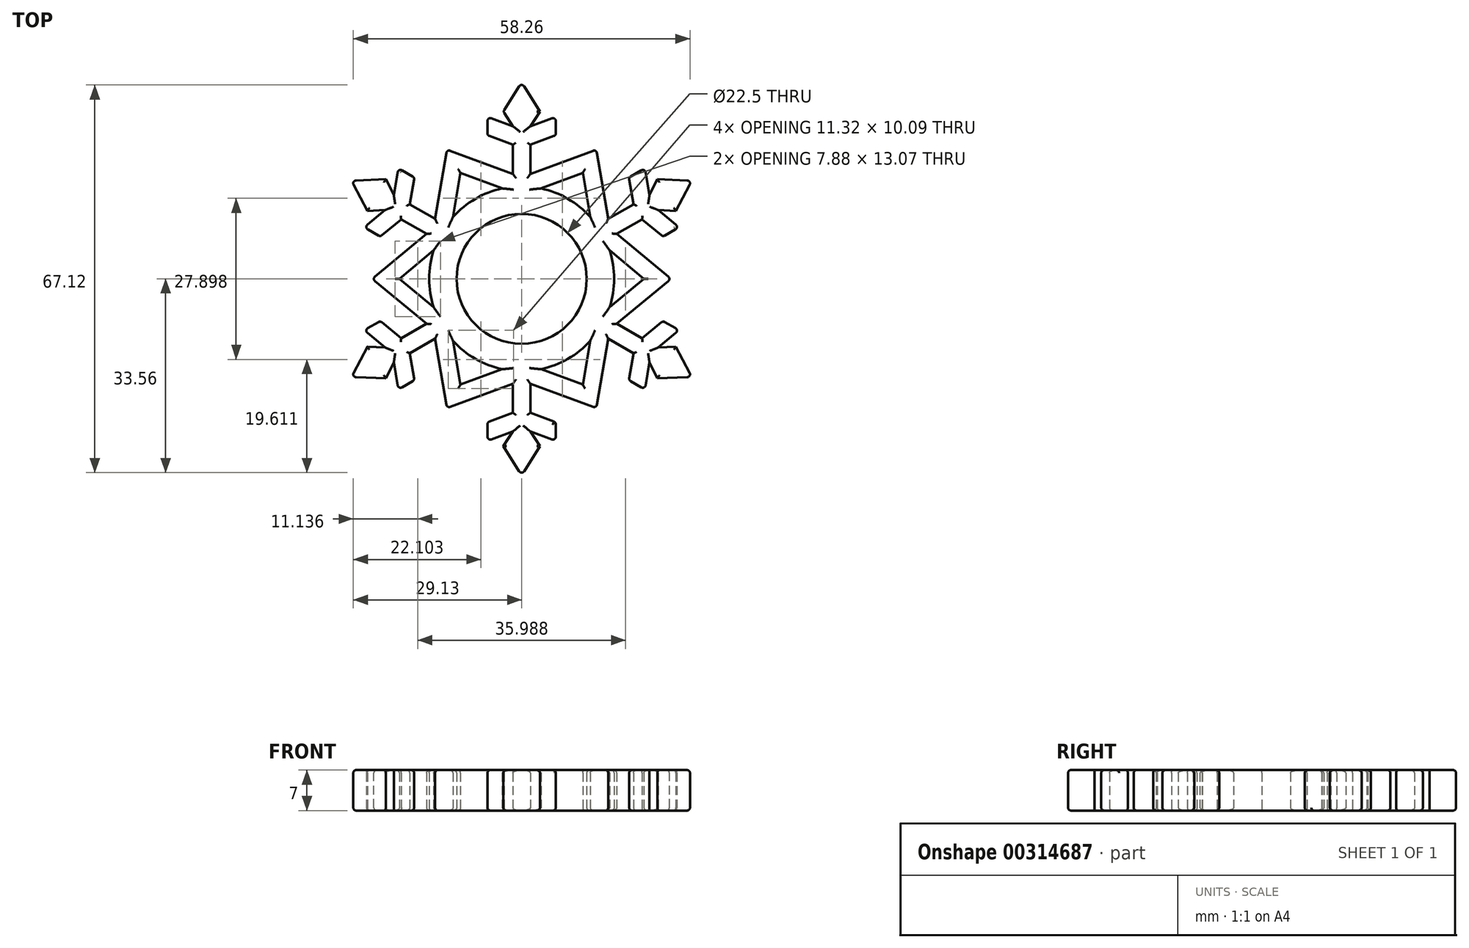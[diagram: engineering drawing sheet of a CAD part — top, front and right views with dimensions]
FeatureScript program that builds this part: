
annotation { "Feature Type Name" : "Feature", "Feature Type Description" : "" }
export const myFeature = defineFeature(function(context is Context, id is Id, definition is map)
    precondition{}
    {
        {
            var Q0;
            Q0=qCreatedBy(makeId("Top.planeOp"),FACE);
            var sketch = newSketch(context, id + "F0", { "sketchPlane" : qUnion([Q0])});
            skCircle(sketch, "E0", {"center": v(0, 0) * mm, "radius": 11.25 * mm});
            skCircle(sketch, "E1", {"center": v(0, 0) * mm, "radius": 16 * mm});
            skCircle(sketch, "E2", {"center": v(0, 0) * mm, "radius": 34 * mm, "construction": true});
            skPoint(sketch, "E3.0.midPoint", {"position": v(19.02, -6.18) * mm});
            skLineSegment(sketch, "E4", {"start": v(29.44, -17) * mm, "end": v(-29.44, 17) * mm, "construction": true});
            skLineSegment(sketch, "E5", {"start": v(29.44, 17) * mm, "end": v(-29.44, -17) * mm, "construction": true});
            skLineSegment(sketch, "E6", {"start": v(0, 34) * mm, "end": v(0, -34) * mm, "construction": true});
            skCircle(sketch, "E7.cCircle", {"center": v(0, 0) * mm, "radius": 23.5 * mm, "construction": true});
            skLineSegment(sketch, "E7.0", {"start": v(11.75, -20.35) * mm, "end": v(-11.75, -20.35) * mm, "construction": true});
            skLineSegment(sketch, "E7.1", {"start": v(-11.75, -20.35) * mm, "end": v(-23.5, 0) * mm, "construction": true});
            skLineSegment(sketch, "E7.2", {"start": v(-23.5, 0) * mm, "end": v(-11.75, 20.35) * mm, "construction": true});
            skLineSegment(sketch, "E7.3", {"start": v(-11.75, 20.35) * mm, "end": v(11.75, 20.35) * mm, "construction": true});
            skLineSegment(sketch, "E7.4", {"start": v(11.75, 20.35) * mm, "end": v(23.5, 0) * mm, "construction": true});
            skLineSegment(sketch, "E7.5", {"start": v(23.5, 0) * mm, "end": v(11.75, -20.35) * mm, "construction": true});
            skLineSegment(sketch, "E8", {"start": v(-11.75, 20.35) * mm, "end": v(0, 16) * mm, "construction": true});
            skLineSegment(sketch, "E9", {"start": v(-12.92, 22.39) * mm, "end": v(0, 17.6) * mm});
            skLineSegment(sketch, "E10", {"start": v(-3.36, 15.64) * mm, "end": v(-10.58, 18.32) * mm});
            skLineSegment(sketch, "E11", {"start": v(-11.75, 20.35) * mm, "end": v(-13.86, 8) * mm, "construction": true});
            skLineSegment(sketch, "E12", {"start": v(-11.87, 10.73) * mm, "end": v(-10.58, 18.32) * mm});
            skLineSegment(sketch, "E13", {"start": v(-12.92, 22.39) * mm, "end": v(-15.24, 8.8) * mm});
            skPoint(sketch, "E14.orphan", {"position": v(-16.07, 20.35) * mm});
            skLineSegment(sketch, "E15.1.0", {"start": v(-25.85, 0) * mm, "end": v(-15.24, -8.8) * mm});
            skLineSegment(sketch, "E15.1.1", {"start": v(-25.85, 0) * mm, "end": v(-15.24, 8.8) * mm});
            skLineSegment(sketch, "E15.1.2", {"start": v(-15.23, 4.91) * mm, "end": v(-21.15, 0) * mm});
            skLineSegment(sketch, "E15.1.3", {"start": v(-15.23, -4.91) * mm, "end": v(-21.15, 0) * mm});
            skLineSegment(sketch, "E15.2.0", {"start": v(-12.92, -22.39) * mm, "end": v(0, -17.6) * mm});
            skLineSegment(sketch, "E15.2.1", {"start": v(-12.92, -22.39) * mm, "end": v(-15.24, -8.8) * mm});
            skLineSegment(sketch, "E15.2.2", {"start": v(-11.87, -10.73) * mm, "end": v(-10.58, -18.32) * mm});
            skLineSegment(sketch, "E15.2.3", {"start": v(-3.36, -15.64) * mm, "end": v(-10.58, -18.32) * mm});
            skLineSegment(sketch, "E16.2.3.0", {"start": v(12.92, -22.39) * mm, "end": v(15.24, -8.8) * mm});
            skLineSegment(sketch, "E16.3.3.0", {"start": v(12.92, -22.39) * mm, "end": v(0, -17.6) * mm});
            skLineSegment(sketch, "E16.6.3.0", {"start": v(3.36, -15.64) * mm, "end": v(10.58, -18.32) * mm});
            skLineSegment(sketch, "E16.9.3.0", {"start": v(11.87, -10.73) * mm, "end": v(10.58, -18.32) * mm});
            skLineSegment(sketch, "E16.2.4.0", {"start": v(25.85, 0) * mm, "end": v(15.24, 8.8) * mm});
            skLineSegment(sketch, "E16.3.4.0", {"start": v(25.85, 0) * mm, "end": v(15.24, -8.8) * mm});
            skLineSegment(sketch, "E16.6.4.0", {"start": v(15.23, -4.91) * mm, "end": v(21.15, 0) * mm});
            skLineSegment(sketch, "E16.9.4.0", {"start": v(15.23, 4.91) * mm, "end": v(21.15, 0) * mm});
            skLineSegment(sketch, "E16.2.5.0", {"start": v(12.92, 22.39) * mm, "end": v(0, 17.6) * mm});
            skLineSegment(sketch, "E16.3.5.0", {"start": v(12.92, 22.39) * mm, "end": v(15.24, 8.8) * mm});
            skLineSegment(sketch, "E16.6.5.0", {"start": v(11.87, 10.73) * mm, "end": v(10.58, 18.32) * mm});
            skLineSegment(sketch, "E16.9.5.0", {"start": v(3.36, 15.64) * mm, "end": v(10.58, 18.32) * mm});
            skLineSegment(sketch, "E17", {"start": v(0, 34) * mm, "end": v(-3.17, 28.97) * mm});
            skLineSegment(sketch, "E18", {"start": v(-3.17, 28.97) * mm, "end": v(-1.5, 26.4) * mm});
            skLineSegment(sketch, "E19", {"start": v(-1.5, 26.4) * mm, "end": v(-5.91, 28.04) * mm});
            skLineSegment(sketch, "E20", {"start": v(-5.91, 28.04) * mm, "end": v(-5.91, 24.84) * mm});
            skLineSegment(sketch, "E21", {"start": v(-5.91, 24.84) * mm, "end": v(-1.5, 23.21) * mm});
            skLineSegment(sketch, "E22", {"start": v(-1.5, 23.21) * mm, "end": v(-1.5, 18.16) * mm});
            skLineSegment(sketch, "E23.MirrorCS", {"start": v(0, 34) * mm, "end": v(3.17, 28.97) * mm});
            skLineSegment(sketch, "E24.MirrorCS", {"start": v(3.17, 28.97) * mm, "end": v(1.5, 26.4) * mm});
            skLineSegment(sketch, "E25.MirrorCS", {"start": v(1.5, 26.4) * mm, "end": v(5.91, 28.04) * mm});
            skLineSegment(sketch, "E26.MirrorCS", {"start": v(5.91, 28.04) * mm, "end": v(5.91, 24.84) * mm});
            skLineSegment(sketch, "E27.MirrorCS", {"start": v(5.91, 24.84) * mm, "end": v(1.5, 23.21) * mm});
            skLineSegment(sketch, "E28.MirrorCS", {"start": v(1.5, 23.21) * mm, "end": v(1.5, 18.16) * mm});
            skLineSegment(sketch, "E29.1.0", {"start": v(-29.44, 17) * mm, "end": v(-26.67, 11.74) * mm});
            skLineSegment(sketch, "E29.1.1", {"start": v(-29.44, 17) * mm, "end": v(-23.5, 17.23) * mm});
            skLineSegment(sketch, "E29.1.2", {"start": v(-23.5, 17.23) * mm, "end": v(-22.12, 14.5) * mm});
            skLineSegment(sketch, "E29.1.3", {"start": v(-26.67, 11.74) * mm, "end": v(-23.62, 11.9) * mm});
            skLineSegment(sketch, "E29.1.4", {"start": v(-23.62, 11.9) * mm, "end": v(-27.24, 8.9) * mm});
            skLineSegment(sketch, "E29.1.5", {"start": v(-27.24, 8.9) * mm, "end": v(-24.47, 7.3) * mm});
            skLineSegment(sketch, "E29.1.6", {"start": v(-24.47, 7.3) * mm, "end": v(-20.85, 10.3) * mm});
            skLineSegment(sketch, "E29.1.7", {"start": v(-20.85, 10.3) * mm, "end": v(-16.47, 7.78) * mm});
            skLineSegment(sketch, "E29.1.8", {"start": v(-19.35, 12.9) * mm, "end": v(-14.97, 10.38) * mm});
            skLineSegment(sketch, "E29.1.9", {"start": v(-18.56, 17.54) * mm, "end": v(-19.35, 12.9) * mm});
            skLineSegment(sketch, "E29.1.10", {"start": v(-21.33, 19.14) * mm, "end": v(-18.56, 17.54) * mm});
            skLineSegment(sketch, "E29.1.11", {"start": v(-22.12, 14.5) * mm, "end": v(-21.33, 19.14) * mm});
            skLineSegment(sketch, "E29.2.0", {"start": v(-29.44, -17) * mm, "end": v(-23.5, -17.23) * mm});
            skLineSegment(sketch, "E29.2.1", {"start": v(-29.44, -17) * mm, "end": v(-26.67, -11.74) * mm});
            skLineSegment(sketch, "E29.2.2", {"start": v(-26.67, -11.74) * mm, "end": v(-23.62, -11.9) * mm});
            skLineSegment(sketch, "E29.2.3", {"start": v(-23.5, -17.23) * mm, "end": v(-22.12, -14.5) * mm});
            skLineSegment(sketch, "E29.2.4", {"start": v(-22.12, -14.5) * mm, "end": v(-21.33, -19.14) * mm});
            skLineSegment(sketch, "E29.2.5", {"start": v(-21.33, -19.14) * mm, "end": v(-18.56, -17.54) * mm});
            skLineSegment(sketch, "E29.2.6", {"start": v(-18.56, -17.54) * mm, "end": v(-19.35, -12.9) * mm});
            skLineSegment(sketch, "E29.2.7", {"start": v(-19.35, -12.9) * mm, "end": v(-14.97, -10.38) * mm});
            skLineSegment(sketch, "E29.2.8", {"start": v(-20.85, -10.3) * mm, "end": v(-16.47, -7.78) * mm});
            skLineSegment(sketch, "E29.2.9", {"start": v(-24.47, -7.3) * mm, "end": v(-20.85, -10.3) * mm});
            skLineSegment(sketch, "E29.2.10", {"start": v(-27.24, -8.9) * mm, "end": v(-24.47, -7.3) * mm});
            skLineSegment(sketch, "E29.2.11", {"start": v(-23.62, -11.9) * mm, "end": v(-27.24, -8.9) * mm});
            skLineSegment(sketch, "E29.3.0", {"start": v(0, -34) * mm, "end": v(3.17, -28.97) * mm});
            skLineSegment(sketch, "E29.3.1", {"start": v(0, -34) * mm, "end": v(-3.17, -28.97) * mm});
            skLineSegment(sketch, "E29.3.2", {"start": v(-3.17, -28.97) * mm, "end": v(-1.5, -26.4) * mm});
            skLineSegment(sketch, "E29.3.3", {"start": v(3.17, -28.97) * mm, "end": v(1.5, -26.4) * mm});
            skLineSegment(sketch, "E29.3.4", {"start": v(1.5, -26.4) * mm, "end": v(5.91, -28.04) * mm});
            skLineSegment(sketch, "E29.3.5", {"start": v(5.91, -28.04) * mm, "end": v(5.91, -24.84) * mm});
            skLineSegment(sketch, "E29.3.6", {"start": v(5.91, -24.84) * mm, "end": v(1.5, -23.21) * mm});
            skLineSegment(sketch, "E29.3.7", {"start": v(1.5, -23.21) * mm, "end": v(1.5, -18.16) * mm});
            skLineSegment(sketch, "E29.3.8", {"start": v(-1.5, -23.21) * mm, "end": v(-1.5, -18.16) * mm});
            skLineSegment(sketch, "E29.3.9", {"start": v(-5.91, -24.84) * mm, "end": v(-1.5, -23.21) * mm});
            skLineSegment(sketch, "E29.3.10", {"start": v(-5.91, -28.04) * mm, "end": v(-5.91, -24.84) * mm});
            skLineSegment(sketch, "E29.3.11", {"start": v(-1.5, -26.4) * mm, "end": v(-5.91, -28.04) * mm});
            skLineSegment(sketch, "E29.4.0", {"start": v(29.44, -17) * mm, "end": v(26.67, -11.74) * mm});
            skLineSegment(sketch, "E29.4.1", {"start": v(29.44, -17) * mm, "end": v(23.5, -17.23) * mm});
            skLineSegment(sketch, "E29.4.2", {"start": v(23.5, -17.23) * mm, "end": v(22.12, -14.5) * mm});
            skLineSegment(sketch, "E29.4.3", {"start": v(26.67, -11.74) * mm, "end": v(23.62, -11.9) * mm});
            skLineSegment(sketch, "E29.4.4", {"start": v(23.62, -11.9) * mm, "end": v(27.24, -8.9) * mm});
            skLineSegment(sketch, "E29.4.5", {"start": v(27.24, -8.9) * mm, "end": v(24.47, -7.3) * mm});
            skLineSegment(sketch, "E29.4.6", {"start": v(24.47, -7.3) * mm, "end": v(20.85, -10.3) * mm});
            skLineSegment(sketch, "E29.4.7", {"start": v(20.85, -10.3) * mm, "end": v(16.47, -7.78) * mm});
            skLineSegment(sketch, "E29.4.8", {"start": v(19.35, -12.9) * mm, "end": v(14.97, -10.38) * mm});
            skLineSegment(sketch, "E29.4.9", {"start": v(18.56, -17.54) * mm, "end": v(19.35, -12.9) * mm});
            skLineSegment(sketch, "E29.4.10", {"start": v(21.33, -19.14) * mm, "end": v(18.56, -17.54) * mm});
            skLineSegment(sketch, "E29.4.11", {"start": v(22.12, -14.5) * mm, "end": v(21.33, -19.14) * mm});
            skLineSegment(sketch, "E29.5.0", {"start": v(29.44, 17) * mm, "end": v(23.5, 17.23) * mm});
            skLineSegment(sketch, "E29.5.1", {"start": v(29.44, 17) * mm, "end": v(26.67, 11.74) * mm});
            skLineSegment(sketch, "E29.5.2", {"start": v(26.67, 11.74) * mm, "end": v(23.62, 11.9) * mm});
            skLineSegment(sketch, "E29.5.3", {"start": v(23.5, 17.23) * mm, "end": v(22.12, 14.5) * mm});
            skLineSegment(sketch, "E29.5.4", {"start": v(22.12, 14.5) * mm, "end": v(21.33, 19.14) * mm});
            skLineSegment(sketch, "E29.5.5", {"start": v(21.33, 19.14) * mm, "end": v(18.56, 17.54) * mm});
            skLineSegment(sketch, "E29.5.6", {"start": v(18.56, 17.54) * mm, "end": v(19.35, 12.9) * mm});
            skLineSegment(sketch, "E29.5.7", {"start": v(19.35, 12.9) * mm, "end": v(14.97, 10.38) * mm});
            skLineSegment(sketch, "E29.5.8", {"start": v(20.85, 10.3) * mm, "end": v(16.47, 7.78) * mm});
            skLineSegment(sketch, "E29.5.9", {"start": v(24.47, 7.3) * mm, "end": v(20.85, 10.3) * mm});
            skLineSegment(sketch, "E29.5.10", {"start": v(27.24, 8.9) * mm, "end": v(24.47, 7.3) * mm});
            skLineSegment(sketch, "E29.5.11", {"start": v(23.62, 11.9) * mm, "end": v(27.24, 8.9) * mm});
            skSolve(sketch);
        }
        {
            var Q0;
            Q0=makeQuery(id+"F0.imprint","IMPRINT",FACE,{"disambiguationData":[TD([[makeQuery(id+"F0.imprint","IMPRINT",EDGE,{"derivedFrom":sQuery(id+"F0.wireOp",EDGE,"E17")}),1.0]])]});
            var Q1;
            {var subQ23=sQuery(id+"F0.wireOp",EDGE,"E10");Q1=makeQuery(id+"F0.imprint","IMPRINT",FACE,{"disambiguationData":[TD([[makeQuery(id+"F0.imprint","IMPRINT",EDGE,{"derivedFrom":subQ23}),-1.0]])]});}
            var Q2;
            Q2=makeQuery(id+"F0.imprint","IMPRINT",FACE,{"disambiguationData":[TD([[makeQuery(id+"F0.imprint","IMPRINT",EDGE,{"derivedFrom":sQuery(id+"F0.wireOp",EDGE,"E0")}),-1.0]])]});
            var Q3;
            Q3=makeQuery(id+"F0.imprint","IMPRINT",FACE,{"disambiguationData":[TD([[makeQuery(id+"F0.imprint","IMPRINT",EDGE,{"derivedFrom":sQuery(id+"F0.wireOp",EDGE,"E29.1.0")}),1.0]])]});
            var Q4;
            Q4=makeQuery(id+"F0.imprint","IMPRINT",FACE,{"disambiguationData":[TD([[makeQuery(id+"F0.imprint","IMPRINT",EDGE,{"derivedFrom":sQuery(id+"F0.wireOp",EDGE,"E29.5.0")}),1.0]])]});
            var Q5;
            Q5=makeQuery(id+"F0.imprint","IMPRINT",FACE,{"disambiguationData":[TD([[makeQuery(id+"F0.imprint","IMPRINT",EDGE,{"derivedFrom":sQuery(id+"F0.wireOp",EDGE,"E29.4.0")}),1.0]])]});
            var Q6;
            Q6=makeQuery(id+"F0.imprint","IMPRINT",FACE,{"disambiguationData":[TD([[makeQuery(id+"F0.imprint","IMPRINT",EDGE,{"derivedFrom":sQuery(id+"F0.wireOp",EDGE,"E29.2.0")}),1.0]])]});
            var Q7;
            Q7=makeQuery(id+"F0.imprint","IMPRINT",FACE,{"disambiguationData":[TD([[makeQuery(id+"F0.imprint","IMPRINT",EDGE,{"derivedFrom":sQuery(id+"F0.wireOp",EDGE,"E29.3.0")}),1.0]])]});
            extrude(context, id + "F1", {"entities" : qUnion([Q0, Q1, Q2, Q3, Q4, Q5, Q6, Q7]), "depth" : 7 * mm, "offsetDistance" : 25 * mm});
        }
        {
            var Q0;
            Q0=makeQuery(id+"F1.opExtrude","SWEPT_EDGE",EDGE,{"disambiguationData":[OSD([sQuery(id+"F0.wireOp",EDGE,"E29.4.0"),sQuery(id+"F0.wireOp",EDGE,"E29.4.1")])]});
            var Q1;
            Q1=makeQuery(id+"F1.opExtrude","SWEPT_EDGE",EDGE,{"disambiguationData":[OSD([sQuery(id+"F0.wireOp",EDGE,"E29.4.4"),sQuery(id+"F0.wireOp",EDGE,"E29.4.5")])]});
            var Q2;
            Q2=makeQuery(id+"F1.opExtrude","SWEPT_EDGE",EDGE,{"disambiguationData":[OSD([sQuery(id+"F0.wireOp",EDGE,"E16.2.4.0"),sQuery(id+"F0.wireOp",EDGE,"E16.3.4.0")])]});
            var Q3;
            Q3=makeQuery(id+"F1.opExtrude","SWEPT_EDGE",EDGE,{"disambiguationData":[OSD([sQuery(id+"F0.wireOp",EDGE,"E29.5.10"),sQuery(id+"F0.wireOp",EDGE,"E29.5.11")])]});
            var Q4;
            Q4=makeQuery(id+"F1.opExtrude","SWEPT_EDGE",EDGE,{"disambiguationData":[OSD([sQuery(id+"F0.wireOp",EDGE,"E29.5.0"),sQuery(id+"F0.wireOp",EDGE,"E29.5.1")])]});
            var Q5;
            Q5=makeQuery(id+"F1.opExtrude","SWEPT_EDGE",EDGE,{"disambiguationData":[OSD([sQuery(id+"F0.wireOp",EDGE,"E29.5.4"),sQuery(id+"F0.wireOp",EDGE,"E29.5.5")])]});
            var Q6;
            Q6=makeQuery(id+"F1.opExtrude","SWEPT_EDGE",EDGE,{"disambiguationData":[OSD([sQuery(id+"F0.wireOp",EDGE,"E16.2.5.0"),sQuery(id+"F0.wireOp",EDGE,"E16.3.5.0")])]});
            var Q7;
            Q7=makeQuery(id+"F1.opExtrude","SWEPT_EDGE",EDGE,{"disambiguationData":[OSD([sQuery(id+"F0.wireOp",EDGE,"E25.MirrorCS"),sQuery(id+"F0.wireOp",EDGE,"E26.MirrorCS")])]});
            var Q8;
            Q8=makeQuery(id+"F1.opExtrude","SWEPT_EDGE",EDGE,{"disambiguationData":[OSD([sQuery(id+"F0.wireOp",EDGE,"E17"),sQuery(id+"F0.wireOp",EDGE,"E23.MirrorCS")])]});
            var Q9;
            Q9=makeQuery(id+"F1.opExtrude","SWEPT_EDGE",EDGE,{"disambiguationData":[OSD([sQuery(id+"F0.wireOp",EDGE,"E17"),sQuery(id+"F0.wireOp",EDGE,"E18")])]});
            var Q10;
            Q10=makeQuery(id+"F1.opExtrude","SWEPT_EDGE",EDGE,{"disambiguationData":[OSD([sQuery(id+"F0.wireOp",EDGE,"E19"),sQuery(id+"F0.wireOp",EDGE,"E20")])]});
            var Q11;
            Q11=makeQuery(id+"F1.opExtrude","SWEPT_EDGE",EDGE,{"disambiguationData":[OSD([sQuery(id+"F0.wireOp",EDGE,"E9"),sQuery(id+"F0.wireOp",EDGE,"E13")])]});
            var Q12;
            Q12=makeQuery(id+"F1.opExtrude","SWEPT_EDGE",EDGE,{"disambiguationData":[OSD([sQuery(id+"F0.wireOp",EDGE,"E29.1.10"),sQuery(id+"F0.wireOp",EDGE,"E29.1.11")])]});
            var Q13;
            Q13=makeQuery(id+"F1.opExtrude","SWEPT_EDGE",EDGE,{"disambiguationData":[OSD([sQuery(id+"F0.wireOp",EDGE,"E29.1.0"),sQuery(id+"F0.wireOp",EDGE,"E29.1.1")])]});
            var Q14;
            Q14=makeQuery(id+"F1.opExtrude","SWEPT_EDGE",EDGE,{"disambiguationData":[OSD([sQuery(id+"F0.wireOp",EDGE,"E29.1.4"),sQuery(id+"F0.wireOp",EDGE,"E29.1.5")])]});
            var Q15;
            Q15=makeQuery(id+"F1.opExtrude","SWEPT_EDGE",EDGE,{"disambiguationData":[OSD([sQuery(id+"F0.wireOp",EDGE,"E15.1.0"),sQuery(id+"F0.wireOp",EDGE,"E15.1.1")])]});
            var Q16;
            Q16=makeQuery(id+"F1.opExtrude","SWEPT_EDGE",EDGE,{"disambiguationData":[OSD([sQuery(id+"F0.wireOp",EDGE,"E29.2.10"),sQuery(id+"F0.wireOp",EDGE,"E29.2.11")])]});
            var Q17;
            Q17=makeQuery(id+"F1.opExtrude","SWEPT_EDGE",EDGE,{"disambiguationData":[OSD([sQuery(id+"F0.wireOp",EDGE,"E29.2.0"),sQuery(id+"F0.wireOp",EDGE,"E29.2.1")])]});
            var Q18;
            Q18=makeQuery(id+"F1.opExtrude","SWEPT_EDGE",EDGE,{"disambiguationData":[OSD([sQuery(id+"F0.wireOp",EDGE,"E29.2.4"),sQuery(id+"F0.wireOp",EDGE,"E29.2.5")])]});
            var Q19;
            Q19=makeQuery(id+"F1.opExtrude","SWEPT_EDGE",EDGE,{"disambiguationData":[OSD([sQuery(id+"F0.wireOp",EDGE,"E15.2.0"),sQuery(id+"F0.wireOp",EDGE,"E15.2.1")])]});
            var Q20;
            Q20=makeQuery(id+"F1.opExtrude","SWEPT_EDGE",EDGE,{"disambiguationData":[OSD([sQuery(id+"F0.wireOp",EDGE,"E29.3.10"),sQuery(id+"F0.wireOp",EDGE,"E29.3.11")])]});
            var Q21;
            Q21=makeQuery(id+"F1.opExtrude","SWEPT_EDGE",EDGE,{"disambiguationData":[OSD([sQuery(id+"F0.wireOp",EDGE,"E29.3.0"),sQuery(id+"F0.wireOp",EDGE,"E29.3.1")])]});
            var Q22;
            Q22=makeQuery(id+"F1.opExtrude","SWEPT_EDGE",EDGE,{"disambiguationData":[OSD([sQuery(id+"F0.wireOp",EDGE,"E29.3.4"),sQuery(id+"F0.wireOp",EDGE,"E29.3.5")])]});
            var Q23;
            Q23=makeQuery(id+"F1.opExtrude","SWEPT_EDGE",EDGE,{"disambiguationData":[OSD([sQuery(id+"F0.wireOp",EDGE,"E16.2.3.0"),sQuery(id+"F0.wireOp",EDGE,"E16.3.3.0")])]});
            var Q24;
            Q24=makeQuery(id+"F1.opExtrude","SWEPT_EDGE",EDGE,{"disambiguationData":[OSD([sQuery(id+"F0.wireOp",EDGE,"E29.4.10"),sQuery(id+"F0.wireOp",EDGE,"E29.4.11")])]});
            var Q25;
            Q25=makeQuery(id+"F1.opExtrude","SWEPT_EDGE",EDGE,{"disambiguationData":[OSD([sQuery(id+"F0.wireOp",EDGE,"E20"),sQuery(id+"F0.wireOp",EDGE,"E21")])]});
            var Q26;
            Q26=makeQuery(id+"F1.opExtrude","SWEPT_EDGE",EDGE,{"disambiguationData":[OSD([sQuery(id+"F0.wireOp",EDGE,"E26.MirrorCS"),sQuery(id+"F0.wireOp",EDGE,"E27.MirrorCS")])]});
            var Q27;
            Q27=makeQuery(id+"F1.opExtrude","SWEPT_EDGE",EDGE,{"disambiguationData":[OSD([sQuery(id+"F0.wireOp",EDGE,"E29.5.5"),sQuery(id+"F0.wireOp",EDGE,"E29.5.6")])]});
            var Q28;
            Q28=makeQuery(id+"F1.opExtrude","SWEPT_EDGE",EDGE,{"disambiguationData":[OSD([sQuery(id+"F0.wireOp",EDGE,"E29.5.9"),sQuery(id+"F0.wireOp",EDGE,"E29.5.10")])]});
            var Q29;
            Q29=makeQuery(id+"F1.opExtrude","SWEPT_EDGE",EDGE,{"disambiguationData":[OSD([sQuery(id+"F0.wireOp",EDGE,"E29.4.5"),sQuery(id+"F0.wireOp",EDGE,"E29.4.6")])]});
            var Q30;
            Q30=makeQuery(id+"F1.opExtrude","SWEPT_EDGE",EDGE,{"disambiguationData":[OSD([sQuery(id+"F0.wireOp",EDGE,"E29.4.9"),sQuery(id+"F0.wireOp",EDGE,"E29.4.10")])]});
            var Q31;
            Q31=makeQuery(id+"F1.opExtrude","SWEPT_EDGE",EDGE,{"disambiguationData":[OSD([sQuery(id+"F0.wireOp",EDGE,"E29.3.5"),sQuery(id+"F0.wireOp",EDGE,"E29.3.6")])]});
            var Q32;
            Q32=makeQuery(id+"F1.opExtrude","SWEPT_EDGE",EDGE,{"disambiguationData":[OSD([sQuery(id+"F0.wireOp",EDGE,"E29.3.9"),sQuery(id+"F0.wireOp",EDGE,"E29.3.10")])]});
            var Q33;
            Q33=makeQuery(id+"F1.opExtrude","SWEPT_EDGE",EDGE,{"disambiguationData":[OSD([sQuery(id+"F0.wireOp",EDGE,"E29.2.5"),sQuery(id+"F0.wireOp",EDGE,"E29.2.6")])]});
            var Q34;
            Q34=makeQuery(id+"F1.opExtrude","SWEPT_EDGE",EDGE,{"disambiguationData":[OSD([sQuery(id+"F0.wireOp",EDGE,"E29.2.9"),sQuery(id+"F0.wireOp",EDGE,"E29.2.10")])]});
            var Q35;
            Q35=makeQuery(id+"F1.opExtrude","SWEPT_EDGE",EDGE,{"disambiguationData":[OSD([sQuery(id+"F0.wireOp",EDGE,"E29.1.9"),sQuery(id+"F0.wireOp",EDGE,"E29.1.10")])]});
            var Q36;
            Q36=makeQuery(id+"F1.opExtrude","SWEPT_EDGE",EDGE,{"disambiguationData":[OSD([sQuery(id+"F0.wireOp",EDGE,"E29.1.5"),sQuery(id+"F0.wireOp",EDGE,"E29.1.6")])]});
            fillet(context, id + "F2", {"entities" : qUnion([Q0, Q1, Q2, Q3, Q4, Q5, Q6, Q7, Q8, Q9, Q10, Q11, Q12, Q13, Q14, Q15, Q16, Q17, Q18, Q19, Q20, Q21, Q22, Q23, Q24, Q25, Q26, Q27, Q28, Q29, Q30, Q31, Q32, Q33, Q34, Q35, Q36]), "radius" : .5 * mm, "tangentPropagation" : true, "allowEdgeOverflow" : false});
        }
        {
            var Q0;
            Q0=makeQuery(id+"F1.opExtrude","CAP_FACE",FACE,{"disambiguationData":[OSD([sQuery(id+"F0.wireOp",EDGE,"E0"),sQuery(id+"F0.wireOp",EDGE,"E1"),sQuery(id+"F0.wireOp",EDGE,"E9"),sQuery(id+"F0.wireOp",EDGE,"E10"),sQuery(id+"F0.wireOp",EDGE,"E12"),sQuery(id+"F0.wireOp",EDGE,"E13"),sQuery(id+"F0.wireOp",EDGE,"E15.1.0"),sQuery(id+"F0.wireOp",EDGE,"E15.1.1"),sQuery(id+"F0.wireOp",EDGE,"E15.1.2"),sQuery(id+"F0.wireOp",EDGE,"E15.1.3"),sQuery(id+"F0.wireOp",EDGE,"E15.2.0"),sQuery(id+"F0.wireOp",EDGE,"E15.2.1"),sQuery(id+"F0.wireOp",EDGE,"E15.2.2"),sQuery(id+"F0.wireOp",EDGE,"E15.2.3"),sQuery(id+"F0.wireOp",EDGE,"E16.2.3.0"),sQuery(id+"F0.wireOp",EDGE,"E16.3.3.0"),sQuery(id+"F0.wireOp",EDGE,"E16.6.3.0"),sQuery(id+"F0.wireOp",EDGE,"E16.9.3.0"),sQuery(id+"F0.wireOp",EDGE,"E16.2.4.0"),sQuery(id+"F0.wireOp",EDGE,"E16.3.4.0"),sQuery(id+"F0.wireOp",EDGE,"E16.6.4.0"),sQuery(id+"F0.wireOp",EDGE,"E16.9.4.0"),sQuery(id+"F0.wireOp",EDGE,"E16.2.5.0"),sQuery(id+"F0.wireOp",EDGE,"E16.3.5.0"),sQuery(id+"F0.wireOp",EDGE,"E16.6.5.0"),sQuery(id+"F0.wireOp",EDGE,"E16.9.5.0"),sQuery(id+"F0.wireOp",EDGE,"E17"),sQuery(id+"F0.wireOp",EDGE,"E18"),sQuery(id+"F0.wireOp",EDGE,"E19"),sQuery(id+"F0.wireOp",EDGE,"E20"),sQuery(id+"F0.wireOp",EDGE,"E21"),sQuery(id+"F0.wireOp",EDGE,"E22"),sQuery(id+"F0.wireOp",EDGE,"E23.MirrorCS"),sQuery(id+"F0.wireOp",EDGE,"E24.MirrorCS"),sQuery(id+"F0.wireOp",EDGE,"E25.MirrorCS"),sQuery(id+"F0.wireOp",EDGE,"E26.MirrorCS"),sQuery(id+"F0.wireOp",EDGE,"E27.MirrorCS"),sQuery(id+"F0.wireOp",EDGE,"E28.MirrorCS"),sQuery(id+"F0.wireOp",EDGE,"E29.1.0"),sQuery(id+"F0.wireOp",EDGE,"E29.1.1"),sQuery(id+"F0.wireOp",EDGE,"E29.1.2"),sQuery(id+"F0.wireOp",EDGE,"E29.1.3"),sQuery(id+"F0.wireOp",EDGE,"E29.1.4"),sQuery(id+"F0.wireOp",EDGE,"E29.1.5"),sQuery(id+"F0.wireOp",EDGE,"E29.1.6"),sQuery(id+"F0.wireOp",EDGE,"E29.1.7"),sQuery(id+"F0.wireOp",EDGE,"E29.1.8"),sQuery(id+"F0.wireOp",EDGE,"E29.1.9"),sQuery(id+"F0.wireOp",EDGE,"E29.1.10"),sQuery(id+"F0.wireOp",EDGE,"E29.1.11"),sQuery(id+"F0.wireOp",EDGE,"E29.2.0"),sQuery(id+"F0.wireOp",EDGE,"E29.2.1"),sQuery(id+"F0.wireOp",EDGE,"E29.2.2"),sQuery(id+"F0.wireOp",EDGE,"E29.2.3"),sQuery(id+"F0.wireOp",EDGE,"E29.2.4"),sQuery(id+"F0.wireOp",EDGE,"E29.2.5"),sQuery(id+"F0.wireOp",EDGE,"E29.2.6"),sQuery(id+"F0.wireOp",EDGE,"E29.2.7"),sQuery(id+"F0.wireOp",EDGE,"E29.2.8"),sQuery(id+"F0.wireOp",EDGE,"E29.2.9"),sQuery(id+"F0.wireOp",EDGE,"E29.2.10"),sQuery(id+"F0.wireOp",EDGE,"E29.2.11"),sQuery(id+"F0.wireOp",EDGE,"E29.3.0"),sQuery(id+"F0.wireOp",EDGE,"E29.3.1"),sQuery(id+"F0.wireOp",EDGE,"E29.3.2"),sQuery(id+"F0.wireOp",EDGE,"E29.3.3"),sQuery(id+"F0.wireOp",EDGE,"E29.3.4"),sQuery(id+"F0.wireOp",EDGE,"E29.3.5"),sQuery(id+"F0.wireOp",EDGE,"E29.3.6"),sQuery(id+"F0.wireOp",EDGE,"E29.3.7"),sQuery(id+"F0.wireOp",EDGE,"E29.3.8"),sQuery(id+"F0.wireOp",EDGE,"E29.3.9"),sQuery(id+"F0.wireOp",EDGE,"E29.3.10"),sQuery(id+"F0.wireOp",EDGE,"E29.3.11"),sQuery(id+"F0.wireOp",EDGE,"E29.4.0"),sQuery(id+"F0.wireOp",EDGE,"E29.4.1"),sQuery(id+"F0.wireOp",EDGE,"E29.4.2"),sQuery(id+"F0.wireOp",EDGE,"E29.4.3"),sQuery(id+"F0.wireOp",EDGE,"E29.4.4"),sQuery(id+"F0.wireOp",EDGE,"E29.4.5"),sQuery(id+"F0.wireOp",EDGE,"E29.4.6"),sQuery(id+"F0.wireOp",EDGE,"E29.4.7"),sQuery(id+"F0.wireOp",EDGE,"E29.4.8"),sQuery(id+"F0.wireOp",EDGE,"E29.4.9"),sQuery(id+"F0.wireOp",EDGE,"E29.4.10"),sQuery(id+"F0.wireOp",EDGE,"E29.4.11"),sQuery(id+"F0.wireOp",EDGE,"E29.5.0"),sQuery(id+"F0.wireOp",EDGE,"E29.5.1"),sQuery(id+"F0.wireOp",EDGE,"E29.5.2"),sQuery(id+"F0.wireOp",EDGE,"E29.5.3"),sQuery(id+"F0.wireOp",EDGE,"E29.5.4"),sQuery(id+"F0.wireOp",EDGE,"E29.5.5"),sQuery(id+"F0.wireOp",EDGE,"E29.5.6"),sQuery(id+"F0.wireOp",EDGE,"E29.5.7"),sQuery(id+"F0.wireOp",EDGE,"E29.5.8"),sQuery(id+"F0.wireOp",EDGE,"E29.5.9"),sQuery(id+"F0.wireOp",EDGE,"E29.5.10"),sQuery(id+"F0.wireOp",EDGE,"E29.5.11")])],"isStart":false});
            var Q1;
            Q1=makeQuery(id+"F1.opExtrude","CAP_FACE",FACE,{"disambiguationData":[OSD([sQuery(id+"F0.wireOp",EDGE,"E0"),sQuery(id+"F0.wireOp",EDGE,"E1"),sQuery(id+"F0.wireOp",EDGE,"E9"),sQuery(id+"F0.wireOp",EDGE,"E10"),sQuery(id+"F0.wireOp",EDGE,"E12"),sQuery(id+"F0.wireOp",EDGE,"E13"),sQuery(id+"F0.wireOp",EDGE,"E15.1.0"),sQuery(id+"F0.wireOp",EDGE,"E15.1.1"),sQuery(id+"F0.wireOp",EDGE,"E15.1.2"),sQuery(id+"F0.wireOp",EDGE,"E15.1.3"),sQuery(id+"F0.wireOp",EDGE,"E15.2.0"),sQuery(id+"F0.wireOp",EDGE,"E15.2.1"),sQuery(id+"F0.wireOp",EDGE,"E15.2.2"),sQuery(id+"F0.wireOp",EDGE,"E15.2.3"),sQuery(id+"F0.wireOp",EDGE,"E16.2.3.0"),sQuery(id+"F0.wireOp",EDGE,"E16.3.3.0"),sQuery(id+"F0.wireOp",EDGE,"E16.6.3.0"),sQuery(id+"F0.wireOp",EDGE,"E16.9.3.0"),sQuery(id+"F0.wireOp",EDGE,"E16.2.4.0"),sQuery(id+"F0.wireOp",EDGE,"E16.3.4.0"),sQuery(id+"F0.wireOp",EDGE,"E16.6.4.0"),sQuery(id+"F0.wireOp",EDGE,"E16.9.4.0"),sQuery(id+"F0.wireOp",EDGE,"E16.2.5.0"),sQuery(id+"F0.wireOp",EDGE,"E16.3.5.0"),sQuery(id+"F0.wireOp",EDGE,"E16.6.5.0"),sQuery(id+"F0.wireOp",EDGE,"E16.9.5.0"),sQuery(id+"F0.wireOp",EDGE,"E17"),sQuery(id+"F0.wireOp",EDGE,"E18"),sQuery(id+"F0.wireOp",EDGE,"E19"),sQuery(id+"F0.wireOp",EDGE,"E20"),sQuery(id+"F0.wireOp",EDGE,"E21"),sQuery(id+"F0.wireOp",EDGE,"E22"),sQuery(id+"F0.wireOp",EDGE,"E23.MirrorCS"),sQuery(id+"F0.wireOp",EDGE,"E24.MirrorCS"),sQuery(id+"F0.wireOp",EDGE,"E25.MirrorCS"),sQuery(id+"F0.wireOp",EDGE,"E26.MirrorCS"),sQuery(id+"F0.wireOp",EDGE,"E27.MirrorCS"),sQuery(id+"F0.wireOp",EDGE,"E28.MirrorCS"),sQuery(id+"F0.wireOp",EDGE,"E29.1.0"),sQuery(id+"F0.wireOp",EDGE,"E29.1.1"),sQuery(id+"F0.wireOp",EDGE,"E29.1.2"),sQuery(id+"F0.wireOp",EDGE,"E29.1.3"),sQuery(id+"F0.wireOp",EDGE,"E29.1.4"),sQuery(id+"F0.wireOp",EDGE,"E29.1.5"),sQuery(id+"F0.wireOp",EDGE,"E29.1.6"),sQuery(id+"F0.wireOp",EDGE,"E29.1.7"),sQuery(id+"F0.wireOp",EDGE,"E29.1.8"),sQuery(id+"F0.wireOp",EDGE,"E29.1.9"),sQuery(id+"F0.wireOp",EDGE,"E29.1.10"),sQuery(id+"F0.wireOp",EDGE,"E29.1.11"),sQuery(id+"F0.wireOp",EDGE,"E29.2.0"),sQuery(id+"F0.wireOp",EDGE,"E29.2.1"),sQuery(id+"F0.wireOp",EDGE,"E29.2.2"),sQuery(id+"F0.wireOp",EDGE,"E29.2.3"),sQuery(id+"F0.wireOp",EDGE,"E29.2.4"),sQuery(id+"F0.wireOp",EDGE,"E29.2.5"),sQuery(id+"F0.wireOp",EDGE,"E29.2.6"),sQuery(id+"F0.wireOp",EDGE,"E29.2.7"),sQuery(id+"F0.wireOp",EDGE,"E29.2.8"),sQuery(id+"F0.wireOp",EDGE,"E29.2.9"),sQuery(id+"F0.wireOp",EDGE,"E29.2.10"),sQuery(id+"F0.wireOp",EDGE,"E29.2.11"),sQuery(id+"F0.wireOp",EDGE,"E29.3.0"),sQuery(id+"F0.wireOp",EDGE,"E29.3.1"),sQuery(id+"F0.wireOp",EDGE,"E29.3.2"),sQuery(id+"F0.wireOp",EDGE,"E29.3.3"),sQuery(id+"F0.wireOp",EDGE,"E29.3.4"),sQuery(id+"F0.wireOp",EDGE,"E29.3.5"),sQuery(id+"F0.wireOp",EDGE,"E29.3.6"),sQuery(id+"F0.wireOp",EDGE,"E29.3.7"),sQuery(id+"F0.wireOp",EDGE,"E29.3.8"),sQuery(id+"F0.wireOp",EDGE,"E29.3.9"),sQuery(id+"F0.wireOp",EDGE,"E29.3.10"),sQuery(id+"F0.wireOp",EDGE,"E29.3.11"),sQuery(id+"F0.wireOp",EDGE,"E29.4.0"),sQuery(id+"F0.wireOp",EDGE,"E29.4.1"),sQuery(id+"F0.wireOp",EDGE,"E29.4.2"),sQuery(id+"F0.wireOp",EDGE,"E29.4.3"),sQuery(id+"F0.wireOp",EDGE,"E29.4.4"),sQuery(id+"F0.wireOp",EDGE,"E29.4.5"),sQuery(id+"F0.wireOp",EDGE,"E29.4.6"),sQuery(id+"F0.wireOp",EDGE,"E29.4.7"),sQuery(id+"F0.wireOp",EDGE,"E29.4.8"),sQuery(id+"F0.wireOp",EDGE,"E29.4.9"),sQuery(id+"F0.wireOp",EDGE,"E29.4.10"),sQuery(id+"F0.wireOp",EDGE,"E29.4.11"),sQuery(id+"F0.wireOp",EDGE,"E29.5.0"),sQuery(id+"F0.wireOp",EDGE,"E29.5.1"),sQuery(id+"F0.wireOp",EDGE,"E29.5.2"),sQuery(id+"F0.wireOp",EDGE,"E29.5.3"),sQuery(id+"F0.wireOp",EDGE,"E29.5.4"),sQuery(id+"F0.wireOp",EDGE,"E29.5.5"),sQuery(id+"F0.wireOp",EDGE,"E29.5.6"),sQuery(id+"F0.wireOp",EDGE,"E29.5.7"),sQuery(id+"F0.wireOp",EDGE,"E29.5.8"),sQuery(id+"F0.wireOp",EDGE,"E29.5.9"),sQuery(id+"F0.wireOp",EDGE,"E29.5.10"),sQuery(id+"F0.wireOp",EDGE,"E29.5.11")])],"isStart":true});
            fillet(context, id + "F3", {"entities" : qUnion([Q0, Q1]), "radius" : .5 * mm, "tangentPropagation" : true, "allowEdgeOverflow" : false});
        }
    });
